# Revit family: Pump_Commercial-Utility_Dewatering-Zoeller-314_Seriesxxx
name_source: partatom
category: Mechanical Equipment
revit_build: Autodesk Revit 2014 (Build: 20130308_1515(x64)
units: mm (PartAtom-declared; Revit-internal decimal feet)

## types (1)
- 314 - 115V/1Ph/1.5HP
    Assembly Code = D2090
    Cooling = Air
    Cord Length = 240"
    Cord Type = Grounded Plug
    Default Elevation = 0"
    Description = High-Capacity Water Mover Series Non-Submersible Utility Pump
    Discharge Diameter = 3/4
    Discharge Radius = 3/8"
    Height = 26"
    Hertz = 60
    Impeller = Engineered Plastic
    Installation Type = Floor Mounted
    Length = 16 1/8"
    Manufacturer = Zoeller
    Material = Cast Iron-Zoeller-Powder Coated Epoxy
    Max Flow @ 1' Hd = 1400 GPM
    Max. Head = 110'(33.5 m)
    Max. Operating Temp. = 104° F (40° C)
    Mechanical Seals = Carbon and ceramic
    Model = 314
    Motor = 1/2
    Motor Protection = Auto reset thermal overload (1ph)
    Operation = Nonautomatic
    Phase = 1
    Price = Prices may vary. Please consult Manufacturer Representative for most up-to-date price list.
    Product Documentation Link = http://cdn.qleapahead.com
    Product Page URL = http://zoellerpumps.com
    Pump Housing = Cast Iron
    Type = 1
    URL = http://www.zoellerpumps.com
    Voltage = 115 V
    Warranty Information = 18 Months (Limited)
    Weight = 17 lbs. (8 kg)
    Width = 12 1/2"

## geometry (parser evidence)
native form markers: Sweep x3
no freeform markers — native parametric forms only
